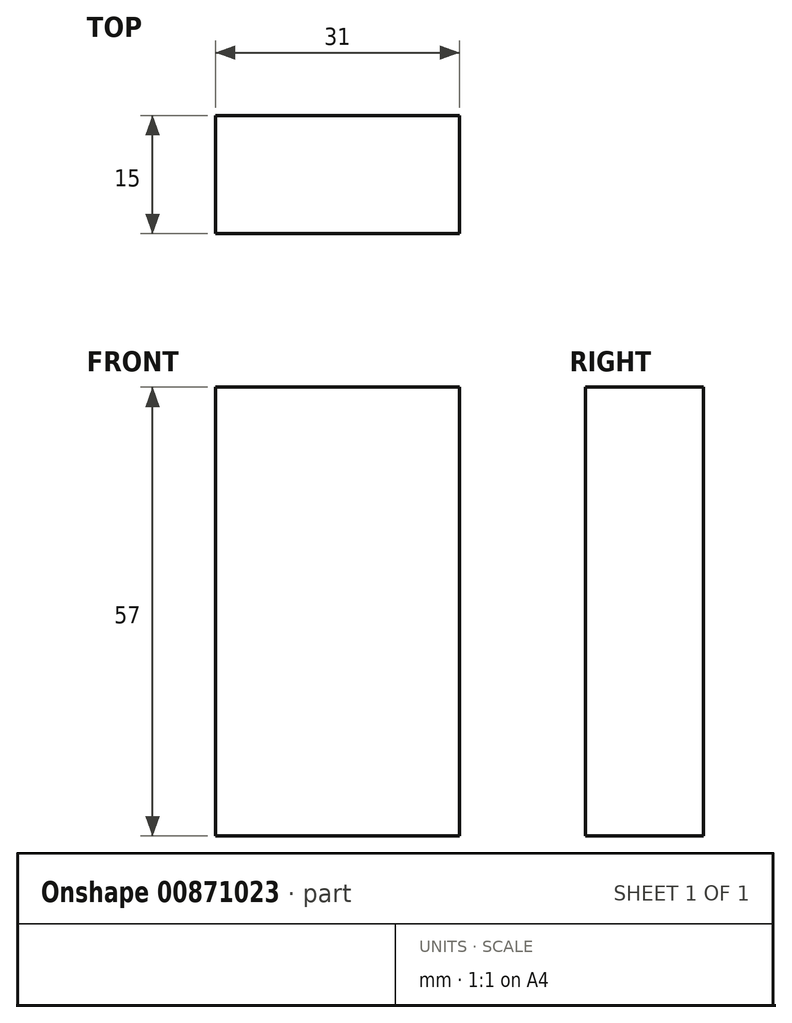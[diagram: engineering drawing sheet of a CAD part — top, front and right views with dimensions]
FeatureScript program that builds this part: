
annotation { "Feature Type Name" : "Feature", "Feature Type Description" : "" }
export const myFeature = defineFeature(function(context is Context, id is Id, definition is map)
    precondition{}
    {
        {
            var Q0;
            Q0=qCreatedBy(makeId("Top.planeOp"),FACE);
            var sketch = newSketch(context, id + "F0", { "sketchPlane" : qUnion([Q0])});
            skLineSegment(sketch, "E0.bottom", {"start": v(-11.95, 9.11) * mm, "end": v(19.05, 9.11) * mm});
            skLineSegment(sketch, "E0.top", {"start": v(-11.95, -5.89) * mm, "end": v(19.05, -5.89) * mm});
            skLineSegment(sketch, "E0.left", {"start": v(-11.95, 9.11) * mm, "end": v(-11.95, -5.89) * mm});
            skLineSegment(sketch, "E0.right", {"start": v(19.05, 9.11) * mm, "end": v(19.05, -5.89) * mm});
            skSolve(sketch);
        }
        {
            var Q0;
            Q0=makeQuery(id+"F0.imprint","IMPRINT",FACE,{"disambiguationData":[TD([[makeQuery(id+"F0.imprint","IMPRINT",EDGE,{"derivedFrom":sQuery(id+"F0.wireOp",EDGE,"E0.bottom")}),-1.0]])]});
            extrude(context, id + "F1", {"entities" : qUnion([Q0]), "depth" : 57 * mm, "offsetDistance" : 25 * mm});
        }
    });
